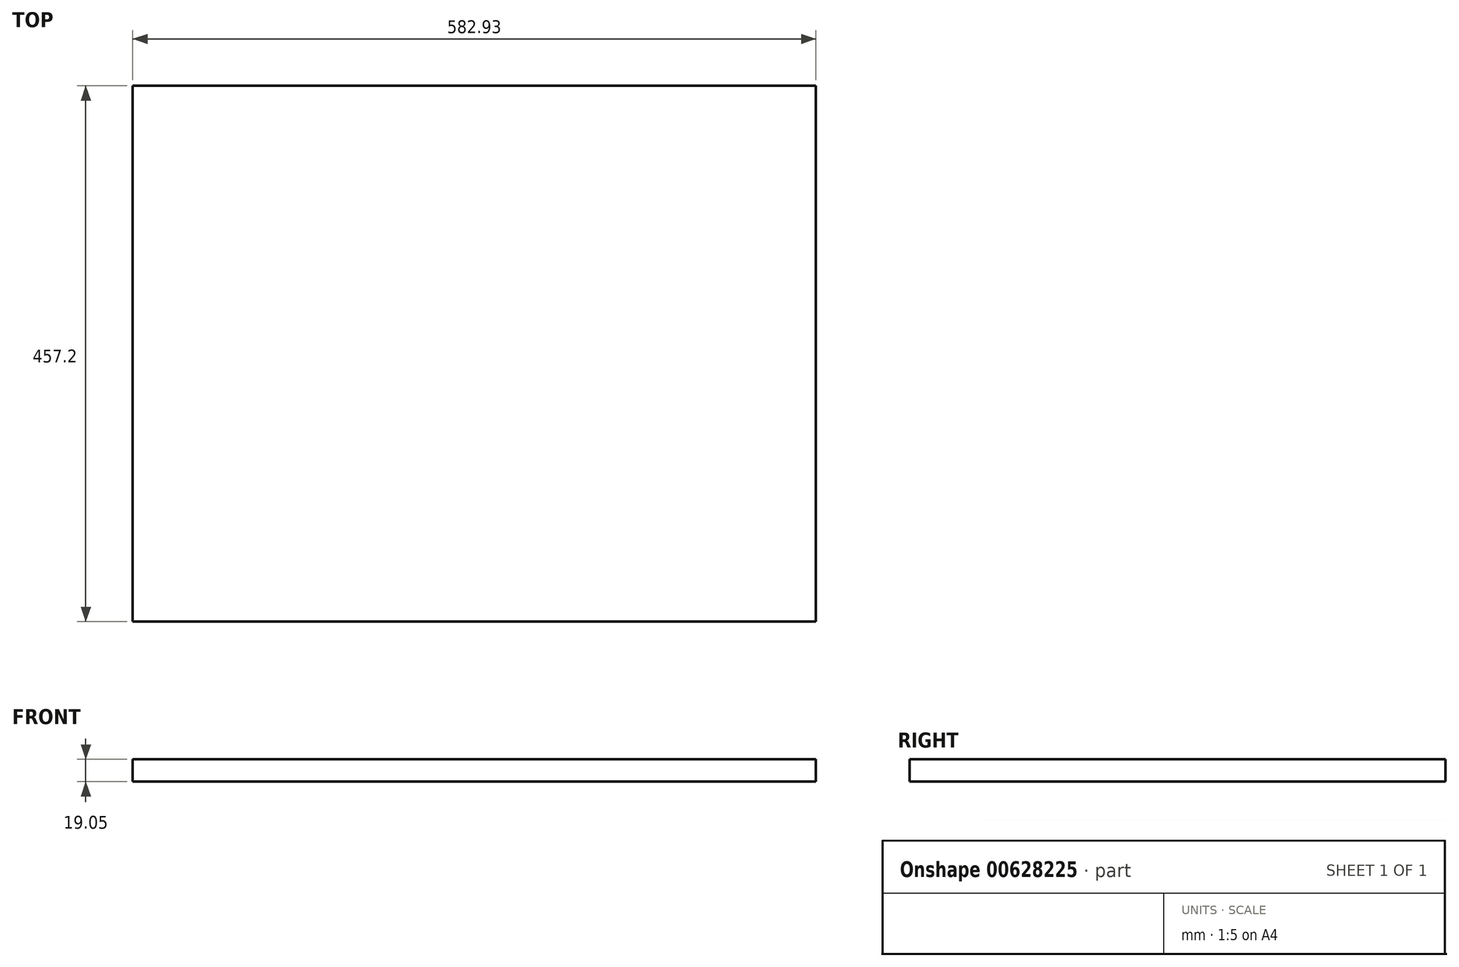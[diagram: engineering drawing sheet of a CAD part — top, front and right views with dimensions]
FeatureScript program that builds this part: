
annotation { "Feature Type Name" : "Feature", "Feature Type Description" : "" }
export const myFeature = defineFeature(function(context is Context, id is Id, definition is map)
    precondition{}
    {
        {
            var Q0;
            Q0=qCreatedBy(makeId("Top.planeOp"),FACE);
            var sketch = newSketch(context, id + "F0", { "sketchPlane" : qUnion([Q0])});
            skLineSegment(sketch, "E0.bottom", {"start": v(0, 0) * mm, "end": v(582.93, 0) * mm});
            skLineSegment(sketch, "E0.top", {"start": v(0, 457.2) * mm, "end": v(582.93, 457.2) * mm});
            skLineSegment(sketch, "E0.left", {"start": v(0, 0) * mm, "end": v(0, 457.2) * mm});
            skLineSegment(sketch, "E0.right", {"start": v(582.93, 0) * mm, "end": v(582.93, 457.2) * mm});
            skSolve(sketch);
        }
        {
            var Q0;
            Q0=makeQuery(id+"F0.imprint","IMPRINT",FACE,{"disambiguationData":[TD([[makeQuery(id+"F0.imprint","IMPRINT",EDGE,{"derivedFrom":sQuery(id+"F0.wireOp",EDGE,"E0.bottom")}),1.0]])]});
            extrude(context, id + "F1", {"entities" : qUnion([Q0]), "depth" : 19.05 * mm, "offsetDistance" : 25.4 * mm});
        }
    });
